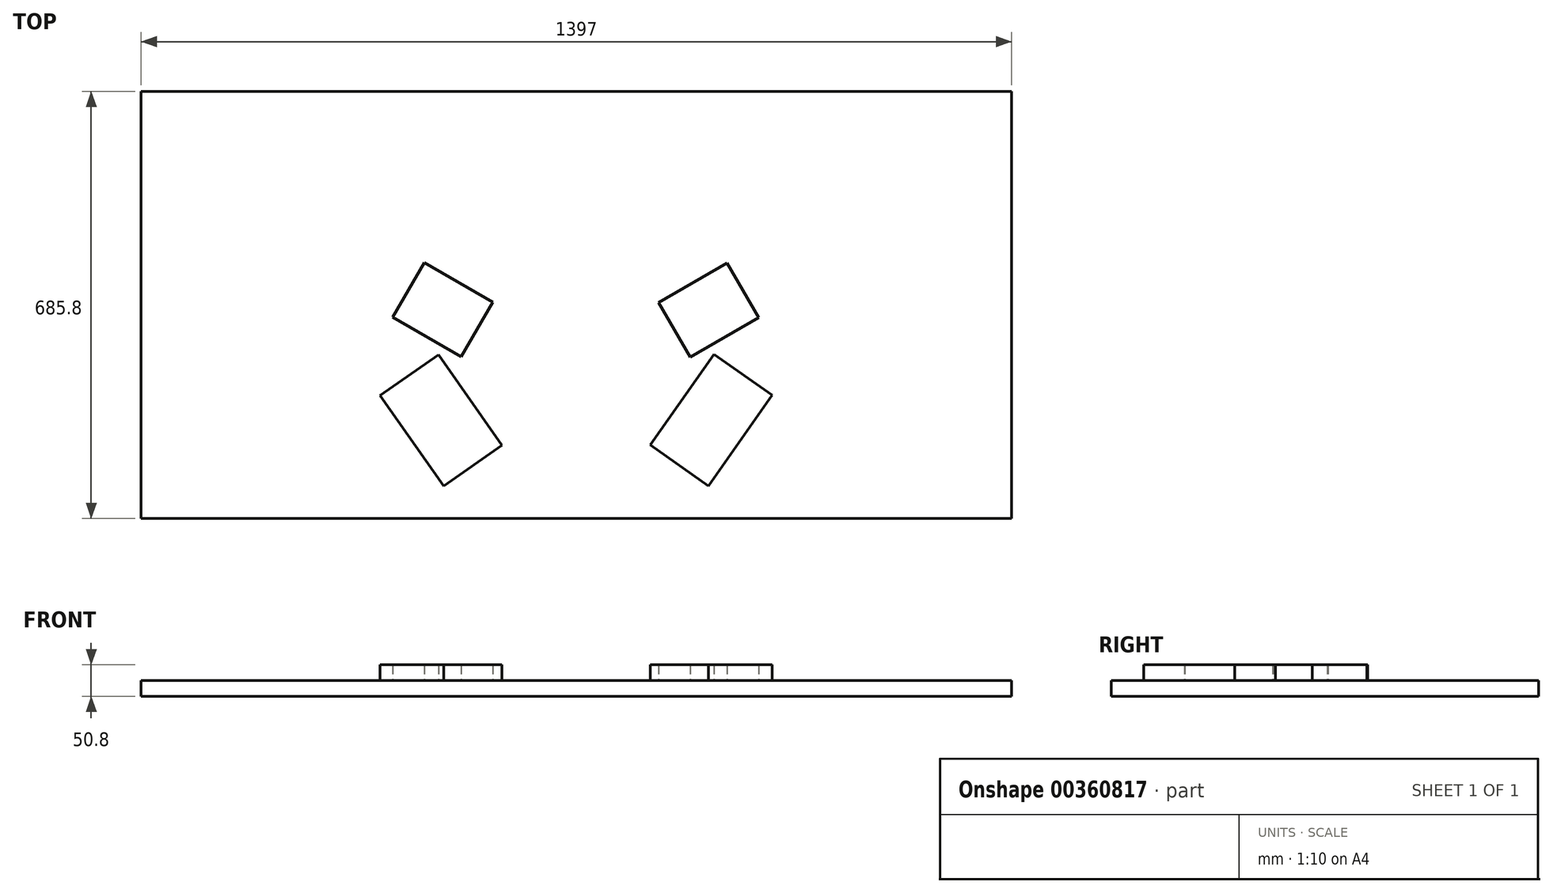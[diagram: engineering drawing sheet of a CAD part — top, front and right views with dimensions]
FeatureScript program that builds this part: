
annotation { "Feature Type Name" : "Feature", "Feature Type Description" : "" }
export const myFeature = defineFeature(function(context is Context, id is Id, definition is map)
    precondition{}
    {
        {
            var Q0;
            Q0=qCreatedBy(makeId("Top.planeOp"),FACE);
            var sketch = newSketch(context, id + "F0", { "sketchPlane" : qUnion([Q0])});
            skLineSegment(sketch, "E0.bottom", {"start": v(698.5, 342.9) * mm, "end": v(-698.5, 342.9) * mm});
            skLineSegment(sketch, "E0.top", {"start": v(698.5, -342.9) * mm, "end": v(-698.5, -342.9) * mm});
            skLineSegment(sketch, "E0.left", {"start": v(698.5, 342.9) * mm, "end": v(698.5, -342.9) * mm});
            skLineSegment(sketch, "E0.right", {"start": v(-698.5, 342.9) * mm, "end": v(-698.5, -342.9) * mm});
            skPoint(sketch, "E0.middle", {"position": v(0, 0) * mm});
            skSolve(sketch);
        }
        {
            var Q0;
            Q0 = qSketchRegion(id + "F0", true);
            extrude(context, id + "F1", {"entities" : qUnion([Q0]), "depth" : 25.4 * mm});
        }
        {
            var Q0;
            Q0=makeQuery(id+"F1.opExtrude","CAP_FACE",FACE,{"disambiguationData":[OSD([sQuery(id+"F0.wireOp",EDGE,"E0.bottom"),sQuery(id+"F0.wireOp",EDGE,"E0.top"),sQuery(id+"F0.wireOp",EDGE,"E0.left"),sQuery(id+"F0.wireOp",EDGE,"E0.right")])],"isStart":false});
            var sketch = newSketch(context, id + "F2", { "sketchPlane" : qUnion([Q0])});
            skLineSegment(sketch, "E1.bottom", {"start": v(101.6, -30.06) * mm, "end": v(-101.6, -30.06) * mm, "construction": true});
            skLineSegment(sketch, "E1.top", {"start": v(101.6, -157.06) * mm, "end": v(-101.6, -157.06) * mm, "construction": true});
            skLineSegment(sketch, "E1.left", {"start": v(101.6, -30.06) * mm, "end": v(101.6, -157.06) * mm, "construction": true});
            skLineSegment(sketch, "E1.right", {"start": v(-101.6, -30.06) * mm, "end": v(-101.6, -157.06) * mm, "construction": true});
            skPoint(sketch, "E1.middle", {"position": v(0, -93.56) * mm});
            skLineSegment(sketch, "E2.bottom", {"start": v(292.56, -20.71) * mm, "end": v(182.58, -84.21) * mm});
            skLineSegment(sketch, "E2.top", {"start": v(241.76, 67.28) * mm, "end": v(131.78, 3.78) * mm});
            skLineSegment(sketch, "E2.left", {"start": v(292.56, -20.71) * mm, "end": v(241.76, 67.28) * mm});
            skLineSegment(sketch, "E2.right", {"start": v(182.58, -84.21) * mm, "end": v(131.78, 3.78) * mm});
            skPoint(sketch, "E2.middle", {"position": v(212.17, -8.47) * mm});
            skLineSegment(sketch, "E3.bottom", {"start": v(212.2, -290.72) * mm, "end": v(118.57, -225.16) * mm});
            skLineSegment(sketch, "E3.top", {"start": v(314.18, -145.08) * mm, "end": v(220.55, -79.52) * mm});
            skLineSegment(sketch, "E3.left", {"start": v(212.2, -290.72) * mm, "end": v(314.18, -145.08) * mm});
            skLineSegment(sketch, "E3.right", {"start": v(118.57, -225.16) * mm, "end": v(220.55, -79.52) * mm});
            skPoint(sketch, "E3.middle", {"position": v(216.38, -185.12) * mm});
            skPoint(sketch, "E4.endSnap0", {"position": v(0, -342.9) * mm});
            skLineSegment(sketch, "E5.MirrorCS", {"start": v(-213.03, -291.08) * mm, "end": v(-315.01, -145.43) * mm});
            skLineSegment(sketch, "E6.MirrorCS", {"start": v(-119.4, -225.52) * mm, "end": v(-221.38, -79.87) * mm});
            skLineSegment(sketch, "E7.MirrorCS", {"start": v(-213.03, -291.08) * mm, "end": v(-119.4, -225.52) * mm});
            skLineSegment(sketch, "E8.MirrorCS", {"start": v(-315.01, -145.43) * mm, "end": v(-221.38, -79.87) * mm});
            skPoint(sketch, "E9.MirrorP", {"position": v(-216.38, -185.12) * mm});
            skLineSegment(sketch, "E10.MirrorCS", {"start": v(-294.72, -19.85) * mm, "end": v(-243.92, 68.14) * mm});
            skPoint(sketch, "E11.MirrorP", {"position": v(-212.17, -8.47) * mm});
            skLineSegment(sketch, "E12.MirrorCS", {"start": v(-294.72, -19.85) * mm, "end": v(-184.74, -83.35) * mm});
            skLineSegment(sketch, "E13.MirrorCS", {"start": v(-243.92, 68.14) * mm, "end": v(-133.94, 4.64) * mm});
            skLineSegment(sketch, "E14.MirrorCS", {"start": v(-184.74, -83.35) * mm, "end": v(-133.94, 4.64) * mm});
            skSolve(sketch);
        }
        {
            var Q0;
            Q0 = qSketchRegion(id + "F2", true);
            extrude(context, id + "F3", {"entities" : qUnion([Q0]), "depth" : 25.4 * mm});
        }
    });
